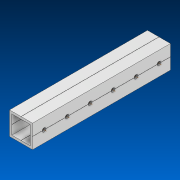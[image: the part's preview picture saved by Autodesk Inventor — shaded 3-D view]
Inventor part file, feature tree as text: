
AUTODESK INVENTOR PART (.ipt)
format: ipt  version: 2022.2 (Build 262287000, 287)  size: 643,584 bytes
history: native  units: in
note: dims shown in document units (in); Inventor stores cm internally (conversion verified against a paired STEP export)
features: other x6, extrude x1, pattern_linear x1, sketch x1, pattern_circular x1
ambient origin geometry x8: Origin, YZ Plane, XZ Plane, XY Plane, X Axis, Y Axis, Z Axis, Center Point
bodies: Solid1 (feature_tree)
feature tree (10):
  extrude  "Extrusion1"  Depth=1.0in
  other  "Work Axis1"
  pattern_linear  "Rectangular Pattern1"  Spacing1=0.0in  [1 undecoded]
  sketch  "Sketch1"  dims[d0=1.0in d1=53.0in d2=0.0in d3=2.3622in d5=1.0in]
  other  "Work Axis2"
  other  "Work Axis3"
  other  "Work Axis4"
  other  "Work Axis5"
  other  "Work Axis6"
  pattern_circular  "CirPattern2"
note: 1 required parameter value undecoded (feature->parameter linkage not recoverable at this tier; creation-order binding heuristic only, values carry confidence <= 0.55)
